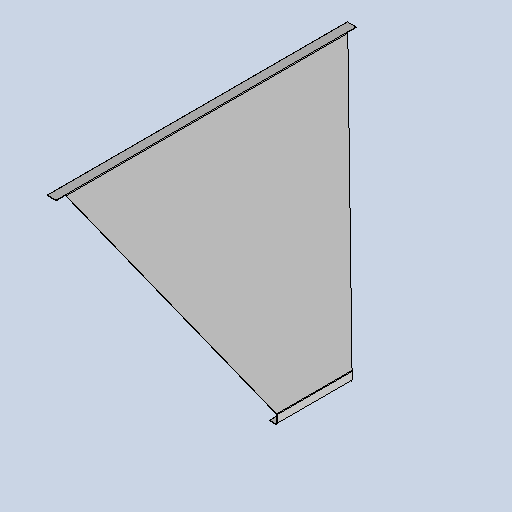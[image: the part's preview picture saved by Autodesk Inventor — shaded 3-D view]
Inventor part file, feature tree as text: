
AUTODESK INVENTOR PART (.ipt)
format: ipt  version: 2025 (Build 290162010, 162A)  size: 314,880 bytes
history: native  units: mm
features: sheet_metal_op x9, other x5, sketch x5, extrude x2, projected_geometry x2, mirror x1
ambient origin geometry x8: Origin, YZ Plane, XZ Plane, XY Plane, X Axis, Y Axis, Z Axis, Center Point
bodies: Body1 (feature_tree)
feature tree (24):
  sheet_metal_op  "Contour Flange2"
  other  "A-Side Definition"
  extrude  "Extrusion14"  Depth=175.0mm
  mirror  "Mirror1"
  extrude  "Extrusion15"  TaperAngle=0.0deg  [1 undecoded]
  sheet_metal_op  "Flange3"
  sheet_metal_op  "Flange4"
  sketch  "Sketch1"  dims[d0=1000.0mm d61=175.0mm]
  other  "Plate4"
  sheet_metal_op  "Bend4"
  sheet_metal_op  "Corner4"
  sketch  "Sketch20"  dims[d66=5.0mm d68=0.0mm]
  projected_geometry  "Projected Loop12"
  sketch  "Sketch21"  dims[d69=3.0mm]
  projected_geometry  "Projected Loop13"
  sketch  "Sketch22"  dims[d70=3.0mm]
  other  "Plate5"
  sheet_metal_op  "Bend5"
  sheet_metal_op  "Corner5"
  sketch  "Sketch23"  dims[d71=1.5mm d72=6.0mm d73=5.0mm d74=1500.0mm d75=5.0mm d76=4.0mm d77=12.0mm d78=3.0mm d79=5.0mm d87=20.666414mm d90=50.0mm d114=50.0mm d115=0.0mm d116=20.926306mm d117=2.0mm d118=2.0mm d119=11.242282mm d120=0.0mm d121=0.0mm d122=400.0mm d123=750.0mm d124=3.0mm d125=1.5mm d126=6.0mm d127=5.0mm d128=50.0mm d129=5.218343mm d130=5.0mm d131=12.0mm d132=3.0mm d133=5.0mm d134=3.0mm d135=1.5mm d136=6.0mm d137=5.0mm d138=40.0mm d139=90.0deg d140=5.0mm d141=12.0mm d142=3.0mm d143=5.0mm]
  other  "Plate6"
  sheet_metal_op  "Bend6"
  sheet_metal_op  "Corner6"
  other  "Definition1"
note: 1 required parameter value undecoded (feature->parameter linkage not recoverable at this tier; creation-order binding heuristic only, values carry confidence <= 0.55)
